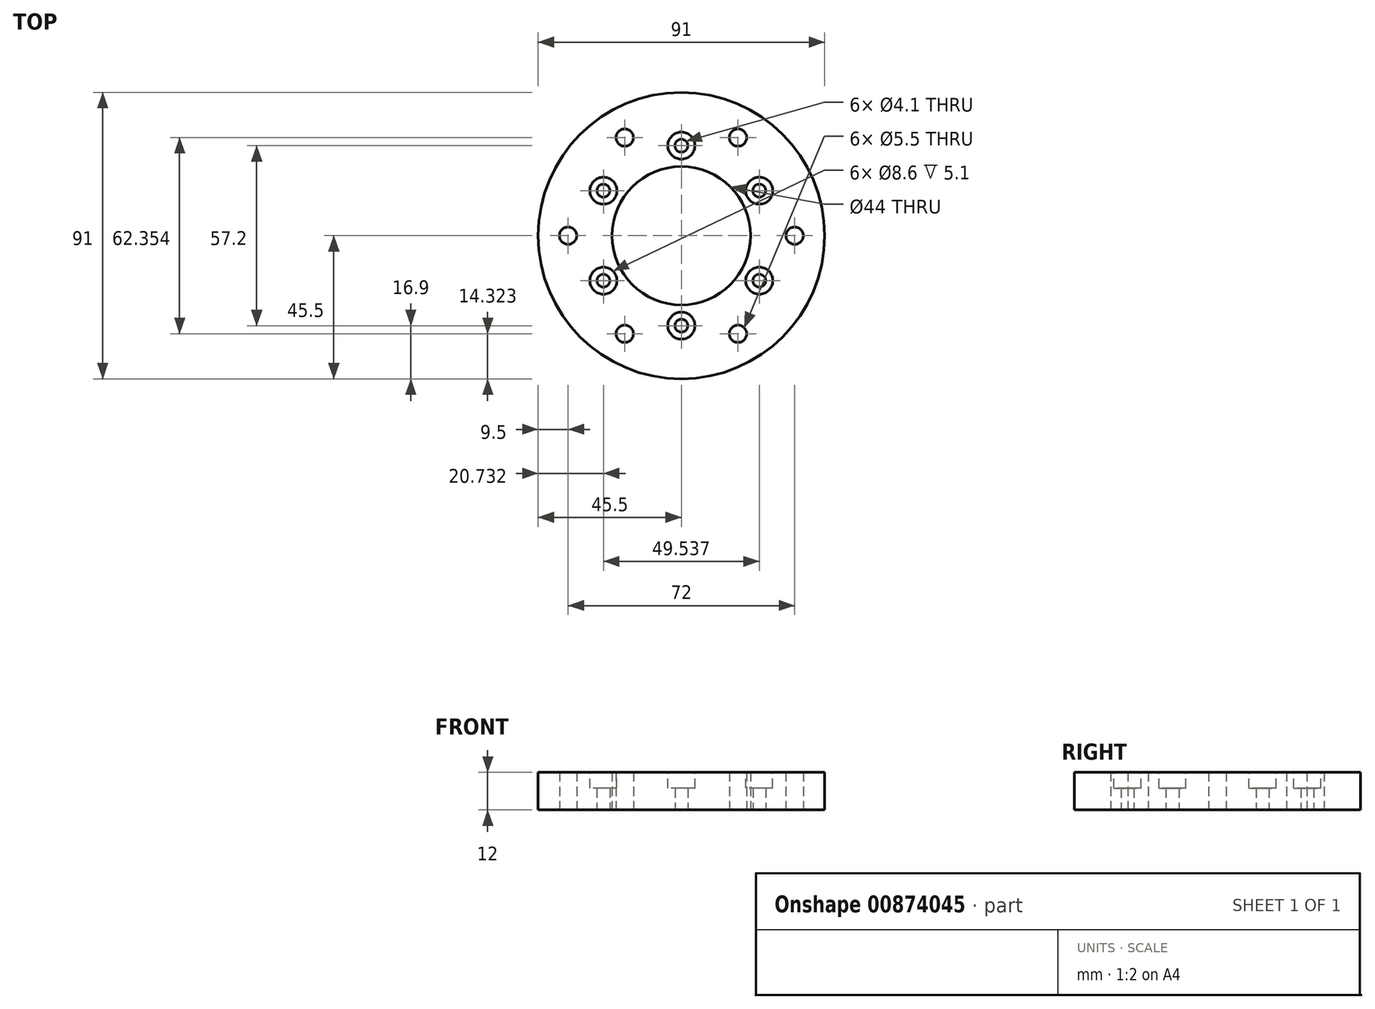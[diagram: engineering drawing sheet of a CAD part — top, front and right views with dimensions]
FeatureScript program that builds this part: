
annotation { "Feature Type Name" : "Feature", "Feature Type Description" : "" }
export const myFeature = defineFeature(function(context is Context, id is Id, definition is map)
    precondition{}
    {
        {
            var Q0;
            Q0=qCreatedBy(makeId("Top.planeOp"),FACE);
            var sketch = newSketch(context, id + "F0", { "sketchPlane" : qUnion([Q0])});
            skCircle(sketch, "E0", {"center": v(0, 0) * mm, "radius": 36 * mm});
            skCircle(sketch, "E1", {"center": v(18, 31.18) * mm, "radius": 2.75 * mm});
            skCircle(sketch, "E2", {"center": v(36, 0) * mm, "radius": 2.75 * mm});
            skCircle(sketch, "E3", {"center": v(-18, 31.18) * mm, "radius": 2.75 * mm});
            skCircle(sketch, "E4", {"center": v(-36, 0) * mm, "radius": 2.75 * mm});
            skCircle(sketch, "E5", {"center": v(-18, -31.18) * mm, "radius": 2.75 * mm});
            skCircle(sketch, "E6", {"center": v(18, -31.18) * mm, "radius": 2.75 * mm});
            skCircle(sketch, "E7", {"center": v(0, 0) * mm, "radius": 45.5 * mm});
            skCircle(sketch, "E8", {"center": v(0, 0) * mm, "radius": 28.6 * mm});
            skCircle(sketch, "E9", {"center": v(0, 28.6) * mm, "radius": 2.05 * mm});
            skCircle(sketch, "E10", {"center": v(24.77, 14.3) * mm, "radius": 2.05 * mm});
            skCircle(sketch, "E11", {"center": v(24.77, -14.3) * mm, "radius": 2.05 * mm});
            skCircle(sketch, "E12", {"center": v(0, -28.6) * mm, "radius": 2.05 * mm});
            skCircle(sketch, "E13", {"center": v(-24.77, -14.3) * mm, "radius": 2.05 * mm});
            skCircle(sketch, "E14", {"center": v(-24.77, 14.3) * mm, "radius": 2.05 * mm});
            skCircle(sketch, "E15", {"center": v(0, 0) * mm, "radius": 22 * mm});
            skSolve(sketch);
        }
        {
            var Q0;
            Q0=makeQuery(id+"F0.imprint","IMPRINT",FACE,{"disambiguationData":[TD([[makeQuery(id+"F0.imprint","IMPRINT",EDGE,{"derivedFrom":sQuery(id+"F0.wireOp",EDGE,"E7")}),1.0]])]});
            var Q1;
            {var subQ20=sQuery(id+"F0.wireOp",EDGE,"E0");var subQ32=sQuery(id+"F0.wireOp",EDGE,"E1");var subQ34=makeQuery(id+"F0.imprint","INTERSECT",VERTEX,{"disambiguationData":[OD(0.0)],"derivedFrom":[subQ20,subQ32]});Q1=makeQuery(id+"F0.imprint","IMPRINT",FACE,{"disambiguationData":[TD([[makeQuery(id+"F0.imprint","IMPRINT",EDGE,{"disambiguationData":[TD([[subQ34,1.0]])],"derivedFrom":subQ20}),1.0]])]});}
            var Q2;
            Q2=makeQuery(id+"F0.imprint","IMPRINT",FACE,{"disambiguationData":[TD([[makeQuery(id+"F0.imprint","IMPRINT",EDGE,{"derivedFrom":sQuery(id+"F0.wireOp",EDGE,"E15")}),-1.0]])]});
            extrude(context, id + "F1", {"entities" : qUnion([Q0, Q1, Q2]), "depth" : 12 * mm, "offsetDistance" : 25 * mm});
        }
        {
            var Q0;
            Q0=makeQuery(id+"F1.opExtrude","CAP_FACE",FACE,{"disambiguationData":[OSD([sQuery(id+"F0.wireOp",EDGE,"E1"),sQuery(id+"F0.wireOp",EDGE,"E2"),sQuery(id+"F0.wireOp",EDGE,"E3"),sQuery(id+"F0.wireOp",EDGE,"E4"),sQuery(id+"F0.wireOp",EDGE,"E5"),sQuery(id+"F0.wireOp",EDGE,"E6"),sQuery(id+"F0.wireOp",EDGE,"E7"),sQuery(id+"F0.wireOp",EDGE,"E9"),sQuery(id+"F0.wireOp",EDGE,"E10"),sQuery(id+"F0.wireOp",EDGE,"E11"),sQuery(id+"F0.wireOp",EDGE,"E12"),sQuery(id+"F0.wireOp",EDGE,"E13"),sQuery(id+"F0.wireOp",EDGE,"E14"),sQuery(id+"F0.wireOp",EDGE,"E15")])],"isStart":false});
            var sketch = newSketch(context, id + "F2", { "sketchPlane" : qUnion([Q0])});
            skCircle(sketch, "E16", {"center": v(0, 0) * mm, "radius": 28.6 * mm});
            skCircle(sketch, "E17", {"center": v(0, 28.6) * mm, "radius": 4.3 * mm});
            skCircle(sketch, "E18", {"center": v(24.77, 14.3) * mm, "radius": 4.3 * mm});
            skCircle(sketch, "E19", {"center": v(24.77, -14.3) * mm, "radius": 4.3 * mm});
            skCircle(sketch, "E20", {"center": v(0, -28.6) * mm, "radius": 4.3 * mm});
            skCircle(sketch, "E21", {"center": v(-24.77, -14.3) * mm, "radius": 4.3 * mm});
            skCircle(sketch, "E22", {"center": v(-24.77, 14.3) * mm, "radius": 4.3 * mm});
            skSolve(sketch);
        }
        {
            var Q0;
            {var subQ0=sQuery(id+"F2.wireOp",EDGE,"E22");var subQ1=sQuery(id+"F2.wireOp",EDGE,"E16");var subQ2=makeQuery(id+"F2.imprint","INTERSECT",VERTEX,{"disambiguationData":[OD(0.0)],"derivedFrom":[subQ1,subQ0]});Q0=makeQuery(id+"F2.imprint","IMPRINT",FACE,{"disambiguationData":[TD([[makeQuery(id+"F2.imprint","IMPRINT",EDGE,{"disambiguationData":[TD([[subQ2,-1.0]])],"derivedFrom":subQ1}),1.0]])]});}
            var Q1;
            {var subQ0=sQuery(id+"F2.wireOp",EDGE,"E22");var subQ1=sQuery(id+"F2.wireOp",EDGE,"E16");var subQ2=makeQuery(id+"F2.imprint","INTERSECT",VERTEX,{"disambiguationData":[OD(0.0)],"derivedFrom":[subQ1,subQ0]});Q1=makeQuery(id+"F2.imprint","IMPRINT",FACE,{"disambiguationData":[TD([[makeQuery(id+"F2.imprint","IMPRINT",EDGE,{"disambiguationData":[TD([[subQ2,-1.0]])],"derivedFrom":subQ1}),-1.0]])]});}
            var Q2;
            {var subQ0=sQuery(id+"F2.wireOp",EDGE,"E17");var subQ1=sQuery(id+"F2.wireOp",EDGE,"E16");var subQ2=makeQuery(id+"F2.imprint","INTERSECT",VERTEX,{"disambiguationData":[OD(0.0)],"derivedFrom":[subQ1,subQ0]});Q2=makeQuery(id+"F2.imprint","IMPRINT",FACE,{"disambiguationData":[TD([[makeQuery(id+"F2.imprint","IMPRINT",EDGE,{"disambiguationData":[TD([[subQ2,-1.0]])],"derivedFrom":subQ1}),-1.0]])]});}
            var Q3;
            {var subQ0=sQuery(id+"F2.wireOp",EDGE,"E17");var subQ1=sQuery(id+"F2.wireOp",EDGE,"E16");var subQ2=makeQuery(id+"F2.imprint","INTERSECT",VERTEX,{"disambiguationData":[OD(0.0)],"derivedFrom":[subQ1,subQ0]});Q3=makeQuery(id+"F2.imprint","IMPRINT",FACE,{"disambiguationData":[TD([[makeQuery(id+"F2.imprint","IMPRINT",EDGE,{"disambiguationData":[TD([[subQ2,-1.0]])],"derivedFrom":subQ1}),1.0]])]});}
            var Q4;
            {var subQ0=sQuery(id+"F2.wireOp",EDGE,"E18");var subQ1=sQuery(id+"F2.wireOp",EDGE,"E16");var subQ2=makeQuery(id+"F2.imprint","INTERSECT",VERTEX,{"disambiguationData":[OD(0.0)],"derivedFrom":[subQ1,subQ0]});Q4=makeQuery(id+"F2.imprint","IMPRINT",FACE,{"disambiguationData":[TD([[makeQuery(id+"F2.imprint","IMPRINT",EDGE,{"disambiguationData":[TD([[subQ2,-1.0]])],"derivedFrom":subQ1}),-1.0]])]});}
            var Q5;
            {var subQ0=sQuery(id+"F2.wireOp",EDGE,"E18");var subQ1=sQuery(id+"F2.wireOp",EDGE,"E16");var subQ2=makeQuery(id+"F2.imprint","INTERSECT",VERTEX,{"disambiguationData":[OD(0.0)],"derivedFrom":[subQ1,subQ0]});Q5=makeQuery(id+"F2.imprint","IMPRINT",FACE,{"disambiguationData":[TD([[makeQuery(id+"F2.imprint","IMPRINT",EDGE,{"disambiguationData":[TD([[subQ2,-1.0]])],"derivedFrom":subQ1}),1.0]])]});}
            var Q6;
            {var subQ0=sQuery(id+"F2.wireOp",EDGE,"E19");var subQ1=sQuery(id+"F2.wireOp",EDGE,"E16");var subQ2=makeQuery(id+"F2.imprint","INTERSECT",VERTEX,{"disambiguationData":[OD(0.0)],"derivedFrom":[subQ1,subQ0]});Q6=makeQuery(id+"F2.imprint","IMPRINT",FACE,{"disambiguationData":[TD([[makeQuery(id+"F2.imprint","IMPRINT",EDGE,{"disambiguationData":[TD([[subQ2,-1.0]])],"derivedFrom":subQ1}),-1.0]])]});}
            var Q7;
            {var subQ0=sQuery(id+"F2.wireOp",EDGE,"E19");var subQ1=sQuery(id+"F2.wireOp",EDGE,"E16");var subQ2=makeQuery(id+"F2.imprint","INTERSECT",VERTEX,{"disambiguationData":[OD(0.0)],"derivedFrom":[subQ1,subQ0]});Q7=makeQuery(id+"F2.imprint","IMPRINT",FACE,{"disambiguationData":[TD([[makeQuery(id+"F2.imprint","IMPRINT",EDGE,{"disambiguationData":[TD([[subQ2,-1.0]])],"derivedFrom":subQ1}),1.0]])]});}
            var Q8;
            {var subQ0=sQuery(id+"F2.wireOp",EDGE,"E20");var subQ1=sQuery(id+"F2.wireOp",EDGE,"E16");var subQ2=makeQuery(id+"F2.imprint","INTERSECT",VERTEX,{"disambiguationData":[OD(0.0)],"derivedFrom":[subQ1,subQ0]});Q8=makeQuery(id+"F2.imprint","IMPRINT",FACE,{"disambiguationData":[TD([[makeQuery(id+"F2.imprint","IMPRINT",EDGE,{"disambiguationData":[TD([[subQ2,-1.0]])],"derivedFrom":subQ1}),1.0]])]});}
            var Q9;
            {var subQ0=sQuery(id+"F2.wireOp",EDGE,"E20");var subQ1=sQuery(id+"F2.wireOp",EDGE,"E16");var subQ2=makeQuery(id+"F2.imprint","INTERSECT",VERTEX,{"disambiguationData":[OD(0.0)],"derivedFrom":[subQ1,subQ0]});Q9=makeQuery(id+"F2.imprint","IMPRINT",FACE,{"disambiguationData":[TD([[makeQuery(id+"F2.imprint","IMPRINT",EDGE,{"disambiguationData":[TD([[subQ2,-1.0]])],"derivedFrom":subQ1}),-1.0]])]});}
            var Q10;
            {var subQ0=sQuery(id+"F2.wireOp",EDGE,"E21");var subQ1=sQuery(id+"F2.wireOp",EDGE,"E16");var subQ2=makeQuery(id+"F2.imprint","INTERSECT",VERTEX,{"disambiguationData":[OD(0.0)],"derivedFrom":[subQ1,subQ0]});Q10=makeQuery(id+"F2.imprint","IMPRINT",FACE,{"disambiguationData":[TD([[makeQuery(id+"F2.imprint","IMPRINT",EDGE,{"disambiguationData":[TD([[subQ2,-1.0]])],"derivedFrom":subQ1}),1.0]])]});}
            var Q11;
            {var subQ0=sQuery(id+"F2.wireOp",EDGE,"E21");var subQ1=sQuery(id+"F2.wireOp",EDGE,"E16");var subQ2=makeQuery(id+"F2.imprint","INTERSECT",VERTEX,{"disambiguationData":[OD(0.0)],"derivedFrom":[subQ1,subQ0]});Q11=makeQuery(id+"F2.imprint","IMPRINT",FACE,{"disambiguationData":[TD([[makeQuery(id+"F2.imprint","IMPRINT",EDGE,{"disambiguationData":[TD([[subQ2,-1.0]])],"derivedFrom":subQ1}),-1.0]])]});}
            extrude(context, id + "F3", {"entities" : qUnion([Q0, Q1, Q2, Q3, Q4, Q5, Q6, Q7, Q8, Q9, Q10, Q11]), "operationType" : NewBodyOperationType.REMOVE, "oppositeDirection" : true, "depth" : 5.1 * mm, "offsetDistance" : 25 * mm});
        }
    });
